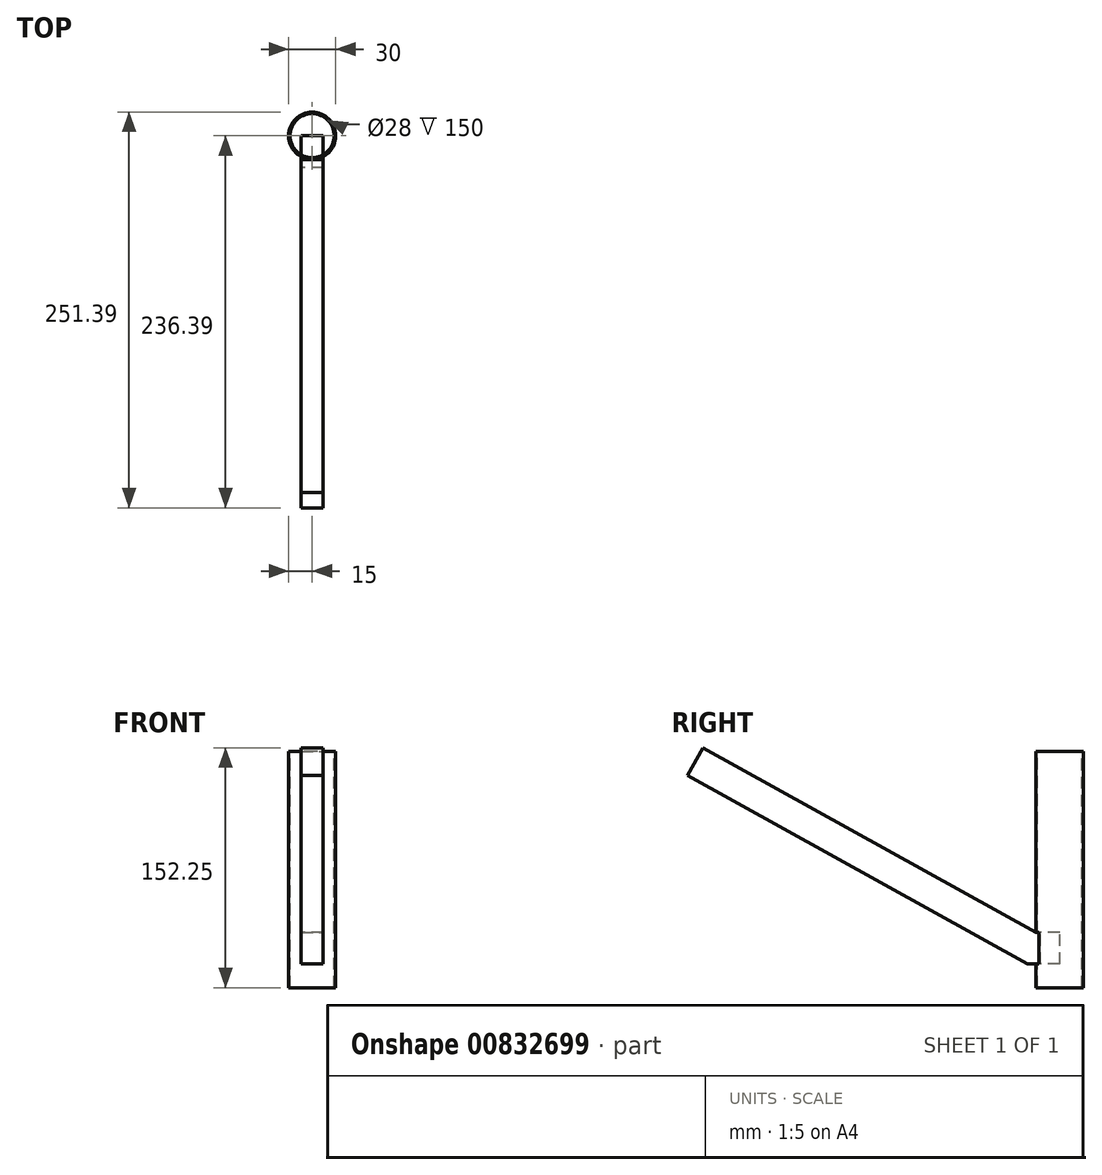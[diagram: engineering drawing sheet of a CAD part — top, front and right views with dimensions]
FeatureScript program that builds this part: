
annotation { "Feature Type Name" : "Feature", "Feature Type Description" : "" }
export const myFeature = defineFeature(function(context is Context, id is Id, definition is map)
    precondition{}
    {
        {
            var Q0;
            Q0=qCreatedBy(makeId("Top.planeOp"),FACE);
            var sketch = newSketch(context, id + "F0", { "sketchPlane" : qUnion([Q0])});
            skCircle(sketch, "E0", {"center": v(0, 0) * mm, "radius": 15 * mm});
            skSolve(sketch);
        }
        {
            var Q0;
            Q0 = qSketchRegion(id + "F0", true);
            extrude(context, id + "F1", {"entities" : qUnion([Q0]), "depth" : 150 * mm, "offsetDistance" : 25 * mm});
        }
        {
            var Q0;
            Q0=makeQuery(id+"F1.opExtrude","CAP_FACE",FACE,{"disambiguationData":[OSD([sQuery(id+"F0.wireOp",EDGE,"E0")])],"isStart":false});
            var sketch = newSketch(context, id + "F2", { "sketchPlane" : qUnion([Q0])});
            skCircle(sketch, "E1", {"center": v(0, 0) * mm, "radius": 14 * mm});
            skSolve(sketch);
        }
        {
            var Q0;
            Q0 = qSketchRegion(id + "F2", true);
            extrude(context, id + "F3", {"entities" : qUnion([Q0]), "operationType" : NewBodyOperationType.REMOVE, "endBound" : BoundingType.UP_TO_NEXT, "oppositeDirection" : true, "depth" : 25 * mm, "offsetDistance" : 25 * mm});
        }
        {
            var Q0;
            Q0=qCreatedBy(makeId("Front.planeOp"),FACE);
            var sketch = newSketch(context, id + "F4", { "sketchPlane" : qUnion([Q0])});
            skLineSegment(sketch, "E2.bottom", {"start": v(7, 15) * mm, "end": v(-7, 15) * mm});
            skLineSegment(sketch, "E2.top", {"start": v(7, 35) * mm, "end": v(-7, 35) * mm});
            skLineSegment(sketch, "E2.left", {"start": v(7, 15) * mm, "end": v(7, 35) * mm});
            skLineSegment(sketch, "E2.right", {"start": v(-7, 15) * mm, "end": v(-7, 35) * mm});
            skSolve(sketch);
        }
        {
            var Q0;
            Q0=qCreatedBy(makeId("Right.planeOp"),FACE);
            var sketch = newSketch(context, id + "F5", { "sketchPlane" : qUnion([Q0])});
            skLineSegment(sketch, "E3", {"start": v(0, 35.69) * mm, "end": v(-15, 35.69) * mm});
            skLineSegment(sketch, "E4", {"start": v(-15, 35.69) * mm, "end": v(-226.36, 152.86) * mm});
            skSolve(sketch);
        }
        {
            var Q0;
            Q0 = qSketchRegion(id + "F4", true);
            var Q1;
            Q1 = qConstructionFilter(qBodyType(qCreatedBy(id + "F5" ,EDGE), BodyType.WIRE), ConstructionObject.NO);
            sweep(context, id + "F6", {"operationType" : NewBodyOperationType.ADD, "profiles" : qUnion([Q0]), "path" : qUnion([Q1])});
        }
        {
            var Q0;
            Q0=qCreatedBy(makeId("Top.planeOp"),FACE);
            var sketch = newSketch(context, id + "F7", { "sketchPlane" : qUnion([Q0])});
            skLineSegment(sketch, "E5", {"start": v(0, 0) * mm, "end": v(75.48, 0) * mm});
            skSolve(sketch);
        }
        {
            var Q0;
            Q0=qCreatedBy(makeId("Front.planeOp"),FACE);
            var Q1;
            Q1 = qBodyType(qCreatedBy(id + "F7" ,EDGE), BodyType.WIRE);
            cPlane(context, id + "F8", {"entities" : qUnion([Q0, Q1]), "cplaneType" : CPlaneType.LINE_ANGLE, "offset" : 25 * mm, "angle" : 30 * degree, "width" : 150 * mm, "height" : 150 * mm});
        }
        {
            var Q0;
            Q0=qCreatedBy(id+"F8.planeOp",FACE);
            var sketch = newSketch(context, id + "F9", { "sketchPlane" : qUnion([Q0])});
            skLineSegment(sketch, "E6.bottom", {"start": v(7, 21.43) * mm, "end": v(-7, 21.43) * mm});
            skLineSegment(sketch, "E6.top", {"start": v(7, 51.43) * mm, "end": v(-7, 51.43) * mm});
            skLineSegment(sketch, "E6.left", {"start": v(7, 21.43) * mm, "end": v(7, 51.43) * mm});
            skLineSegment(sketch, "E6.right", {"start": v(-7, 21.43) * mm, "end": v(-7, 51.43) * mm});
            skLineSegment(sketch, "E7", {"start": v(0, 0) * mm, "end": v(0, 75.79) * mm});
            skSolve(sketch);
        }
        {
            var Q0;
            Q0 = qSketchRegion(id + "F9", true);
            extrude(context, id + "F10", {"entities" : qUnion([Q0]), "depth" : 250 * mm, "offsetDistance" : 25 * mm});
        }
        {
            var Q0;
            Q0=makeQuery(id+"F1.opExtrude","SWEPT_BODY",BODY,{"disambiguationData":[OSD([sQuery(id+"F0.wireOp",EDGE,"E0")])]});
            var Q1;
            Q1=makeQuery(id+"F10.opExtrude","SWEPT_BODY",BODY,{"disambiguationData":[OSD([sQuery(id+"F9.wireOp",EDGE,"E6.bottom"),sQuery(id+"F9.wireOp",EDGE,"E6.top"),sQuery(id+"F9.wireOp",EDGE,"E6.left"),sQuery(id+"F9.wireOp",EDGE,"E6.right")])]});
            booleanBodies(context, id + "F11", {"operationType" : BooleanOperationType.SUBTRACTION, "tools" : qUnion([Q0]), "targets" : qUnion([Q1]), "keepTools" : true});
        }
        {
            var Q0;
            Q0=makeQuery(id+"F11.opBoolean","SPLIT",BODY,{"disambiguationData":[OD(2.0)],"derivedFrom":makeQuery(id+"F10.opExtrude","SWEPT_BODY",BODY,{"disambiguationData":[OSD([sQuery(id+"F9.wireOp",EDGE,"E6.bottom"),sQuery(id+"F9.wireOp",EDGE,"E6.top"),sQuery(id+"F9.wireOp",EDGE,"E6.left"),sQuery(id+"F9.wireOp",EDGE,"E6.right")])]})});
            var Q1;
            Q1=makeQuery(id+"F11.opBoolean","SPLIT",BODY,{"disambiguationData":[OD(3.0)],"derivedFrom":makeQuery(id+"F10.opExtrude","SWEPT_BODY",BODY,{"disambiguationData":[OSD([sQuery(id+"F9.wireOp",EDGE,"E6.bottom"),sQuery(id+"F9.wireOp",EDGE,"E6.top"),sQuery(id+"F9.wireOp",EDGE,"E6.left"),sQuery(id+"F9.wireOp",EDGE,"E6.right")])]})});
            deleteBodies(context, id + "F12", {"entities" : qUnion([Q0, Q1])});
        }
    });
